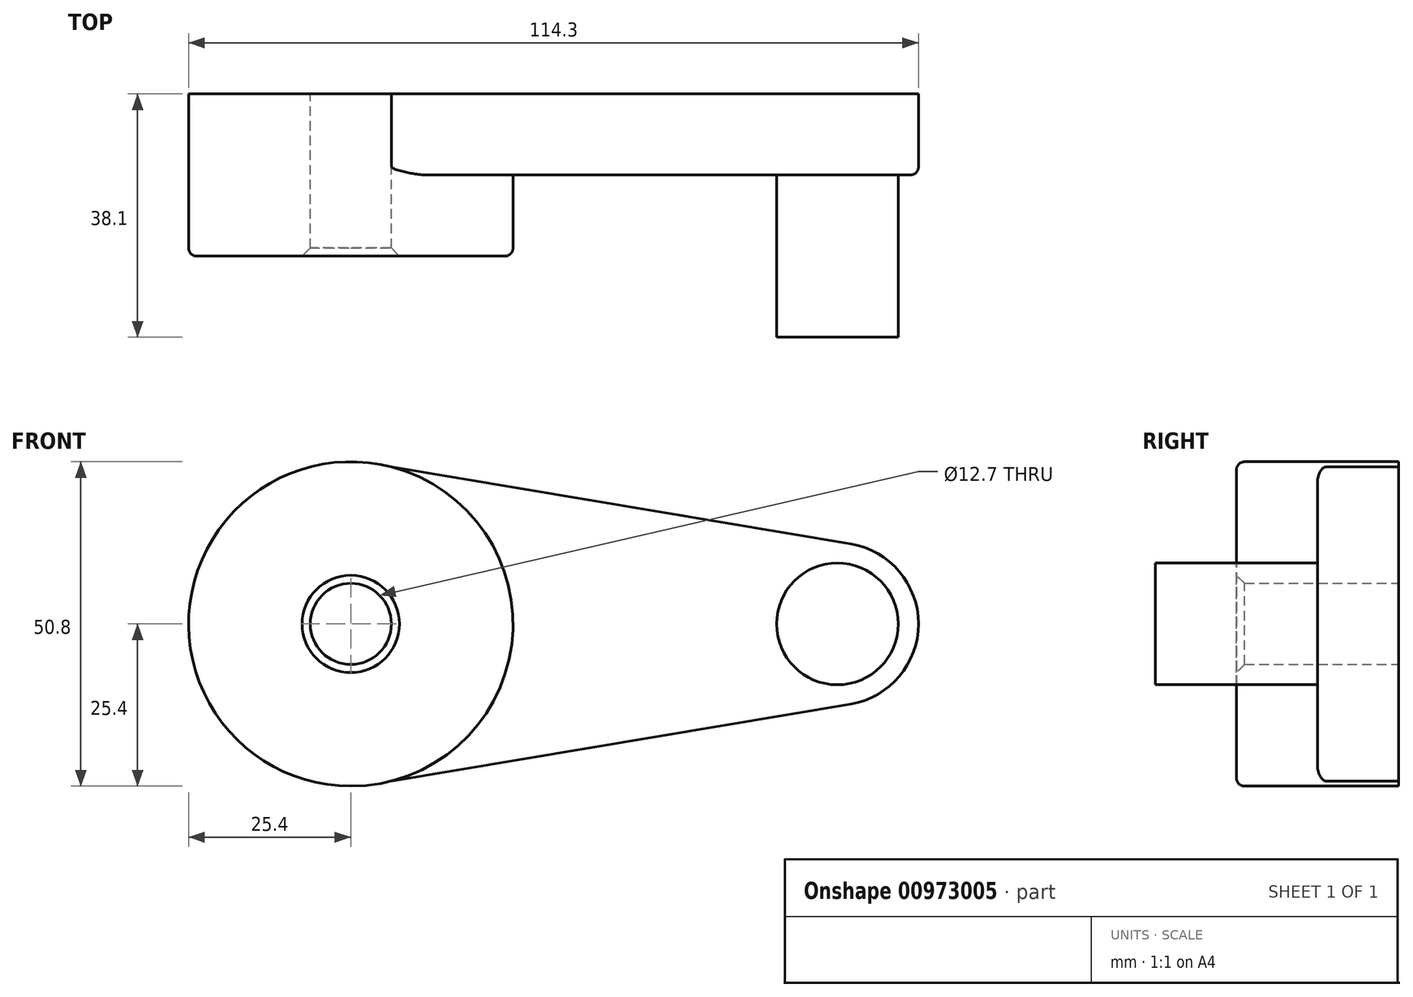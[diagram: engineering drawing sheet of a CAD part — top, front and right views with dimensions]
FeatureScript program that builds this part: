
annotation { "Feature Type Name" : "Feature", "Feature Type Description" : "" }
export const myFeature = defineFeature(function(context is Context, id is Id, definition is map)
    precondition{}
    {
        {
            var Q0;
            Q0=qCreatedBy(makeId("Front.planeOp"),FACE);
            var sketch = newSketch(context, id + "F0", { "sketchPlane" : qUnion([Q0])});
            skCircle(sketch, "E0", {"center": v(0, 0) * mm, "radius": 25.4 * mm});
            skCircle(sketch, "E1", {"center": v(76.2, 0) * mm, "radius": 12.7 * mm});
            skLineSegment(sketch, "E2", {"start": v(6.38, -24.59) * mm, "end": v(78.3, -12.53) * mm});
            skLineSegment(sketch, "E3.MirrorCS", {"start": v(6.38, 24.59) * mm, "end": v(78.3, 12.53) * mm});
            skCircle(sketch, "E4", {"center": v(0, 0) * mm, "radius": 6.35 * mm});
            skCircle(sketch, "E5", {"center": v(76.2, 0) * mm, "radius": 6.35 * mm});
            skCircle(sketch, "E6", {"center": v(76.2, 0) * mm, "radius": 9.53 * mm});
            skSolve(sketch);
        }
        {
            var Q0;
            Q0=makeQuery(id+"F0.imprint","IMPRINT",FACE,{"disambiguationData":[TD([[makeQuery(id+"F0.imprint","IMPRINT",EDGE,{"derivedFrom":sQuery(id+"F0.wireOp",EDGE,"E4")}),-1.0]])]});
            var Q1;
            {var subQ0=sQuery(id+"F0.wireOp",EDGE,"E2");Q1=makeQuery(id+"F0.imprint","IMPRINT",FACE,{"disambiguationData":[TD([[makeQuery(id+"F0.imprint","IMPRINT",EDGE,{"derivedFrom":subQ0}),1.0]])]});}
            var Q2;
            Q2=makeQuery(id+"F0.imprint","IMPRINT",FACE,{"disambiguationData":[TD([[makeQuery(id+"F0.imprint","IMPRINT",EDGE,{"derivedFrom":sQuery(id+"F0.wireOp",EDGE,"E5")}),-1.0]])]});
            var Q3;
            Q3=makeQuery(id+"F0.imprint","IMPRINT",FACE,{"disambiguationData":[TD([[makeQuery(id+"F0.imprint","IMPRINT",EDGE,{"derivedFrom":sQuery(id+"F0.wireOp",EDGE,"E6")}),-1.0]])]});
            extrude(context, id + "F1", {"entities" : qUnion([Q0, Q1, Q2, Q3]), "depth" : 12.7 * mm, "offsetDistance" : 25.4 * mm});
        }
        {
            var Q0;
            Q0=makeQuery(id+"F0.imprint","IMPRINT",FACE,{"disambiguationData":[TD([[makeQuery(id+"F0.imprint","IMPRINT",EDGE,{"derivedFrom":sQuery(id+"F0.wireOp",EDGE,"E4")}),-1.0]])]});
            extrude(context, id + "F2", {"entities" : qUnion([Q0]), "operationType" : NewBodyOperationType.ADD, "depth" : 25.4 * mm, "offsetDistance" : 25.4 * mm});
        }
        {
            var Q0;
            Q0=makeQuery(id+"F1.opExtrude","CAP_EDGE",EDGE,{"disambiguationData":[OSD([sQuery(id+"F0.wireOp",EDGE,"E2")])],"isStart":false});
            var Q1;
            Q1=makeQuery(id+"F2.opExtrude","CAP_EDGE",EDGE,{"disambiguationData":[OSD([sQuery(id+"F0.wireOp",EDGE,"E0")])],"isStart":false});
            fillet(context, id + "F3", {"entities" : qUnion([Q0, Q1]), "radius" : 1.27 * mm, "tangentPropagation" : true, "allowEdgeOverflow" : false});
        }
        {
            var Q0;
            Q0=makeQuery(id+"F2.opExtrude","CAP_EDGE",EDGE,{"disambiguationData":[OSD([sQuery(id+"F0.wireOp",EDGE,"E4")])],"isStart":false});
            chamfer(context, id + "F4", {"entities" : qUnion([Q0]), "width" : 1.27 * mm, "tangentPropagation" : true});
        }
        {
            var Q0;
            Q0=makeQuery(id+"F0.imprint","IMPRINT",FACE,{"disambiguationData":[TD([[makeQuery(id+"F0.imprint","IMPRINT",EDGE,{"derivedFrom":sQuery(id+"F0.wireOp",EDGE,"E5")}),-1.0]])]});
            var Q1;
            Q1=makeQuery(id+"F0.imprint","IMPRINT",FACE,{"disambiguationData":[TD([[makeQuery(id+"F0.imprint","IMPRINT",EDGE,{"derivedFrom":sQuery(id+"F0.wireOp",EDGE,"E5")}),1.0]])]});
            extrude(context, id + "F5", {"entities" : qUnion([Q0, Q1]), "operationType" : NewBodyOperationType.ADD, "depth" : 38.1 * mm, "offsetDistance" : 25.4 * mm});
        }
    });
